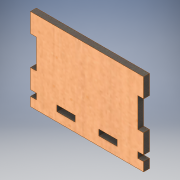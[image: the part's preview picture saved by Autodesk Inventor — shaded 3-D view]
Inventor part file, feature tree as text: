
AUTODESK INVENTOR PART (.ipt)
format: ipt  version: 2019 (Build 230136000, 136)  size: 160,768 bytes
history: native  units: mm
features: other x1, extrude x1, sketch x1
ambient origin geometry x8: Origin, YZ Plane, XZ Plane, XY Plane, X Axis, Y Axis, Z Axis, Center Point
bodies: Body1 (feature_tree)
feature tree (3):
  other  "Твердое тело1"
  extrude  "Выдавливание1"  Depth=4.0mm
  sketch  "Эскиз1"
